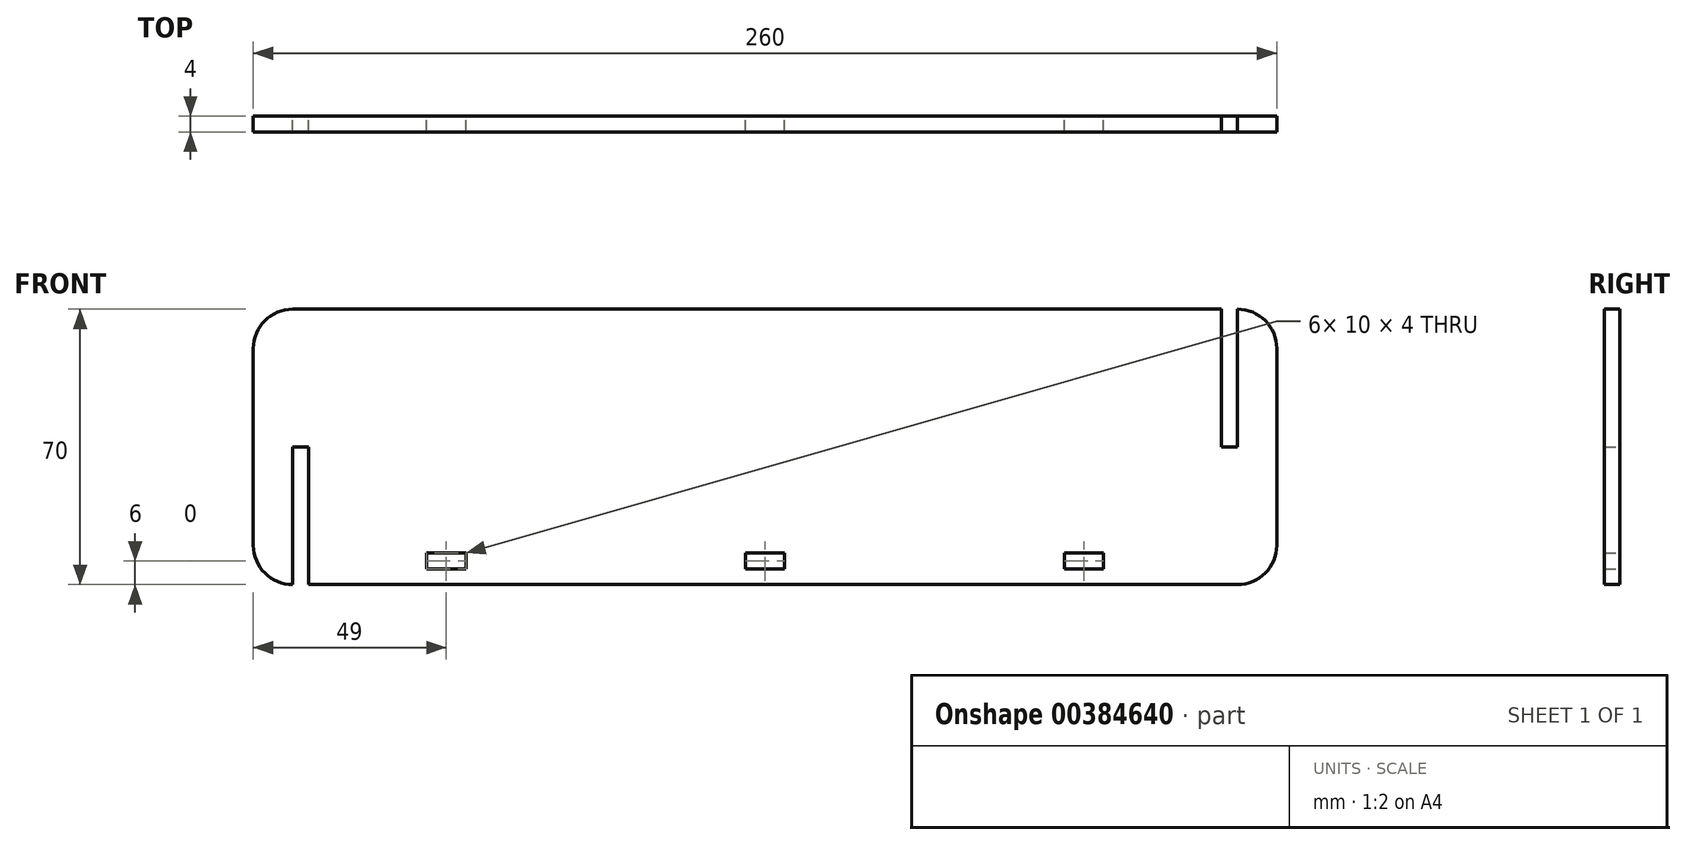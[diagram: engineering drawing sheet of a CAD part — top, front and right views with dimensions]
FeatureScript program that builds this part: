
annotation { "Feature Type Name" : "Feature", "Feature Type Description" : "" }
export const myFeature = defineFeature(function(context is Context, id is Id, definition is map)
    precondition{}
    {
        {
            var Q0;
            Q0=qCreatedBy(makeId("Front.planeOp"),FACE);
            var sketch = newSketch(context, id + "F0", { "sketchPlane" : qUnion([Q0])});
            skLineSegment(sketch, "E0.bottom", {"start": v(-120, 35) * mm, "end": v(116, 35) * mm});
            skLineSegment(sketch, "E0.top", {"start": v(-116, -35) * mm, "end": v(120, -35) * mm});
            skLineSegment(sketch, "E0.left", {"start": v(-130, 25) * mm, "end": v(-130, -25) * mm});
            skLineSegment(sketch, "E0.right", {"start": v(130, 25) * mm, "end": v(130, -25) * mm});
            skPoint(sketch, "E1.visualSharp", {"position": v(-130, 35) * mm});
            skArc(sketch, "E1.filletArc", {"start": v(-120, 35) * mm, "mid": v(-127.07, 32.07) * mm, "end": v(-130, 25) * mm});
            skPoint(sketch, "E2.visualSharp", {"position": v(-130, -35) * mm});
            skArc(sketch, "E2.filletArc", {"start": v(-130, -25) * mm, "mid": v(-127.07, -32.07) * mm, "end": v(-120, -35) * mm});
            skPoint(sketch, "E3.visualSharp", {"position": v(130, -35) * mm});
            skArc(sketch, "E3.filletArc", {"start": v(120, -35) * mm, "mid": v(127.07, -32.07) * mm, "end": v(130, -25) * mm});
            skPoint(sketch, "E4.visualSharp", {"position": v(130, 35) * mm});
            skArc(sketch, "E4.filletArc", {"start": v(130, 25) * mm, "mid": v(127.07, 32.07) * mm, "end": v(120, 35) * mm});
            skLineSegment(sketch, "E5.top", {"start": v(-120, 0) * mm, "end": v(-116, 0) * mm});
            skLineSegment(sketch, "E5.left", {"start": v(-120, -35) * mm, "end": v(-120, 0) * mm});
            skLineSegment(sketch, "E5.right", {"start": v(-116, -35) * mm, "end": v(-116, 0) * mm});
            skLineSegment(sketch, "E6.top", {"start": v(120, 0) * mm, "end": v(116, 0) * mm});
            skLineSegment(sketch, "E6.left", {"start": v(120, 35) * mm, "end": v(120, 0) * mm});
            skLineSegment(sketch, "E6.right", {"start": v(116, 35) * mm, "end": v(116, 0) * mm});
            skLineSegment(sketch, "E7.bottom", {"start": v(-86, -27) * mm, "end": v(-76, -27) * mm});
            skLineSegment(sketch, "E7.top", {"start": v(-86, -31) * mm, "end": v(-76, -31) * mm});
            skLineSegment(sketch, "E7.left", {"start": v(-86, -27) * mm, "end": v(-86, -31) * mm});
            skLineSegment(sketch, "E7.right", {"start": v(-76, -27) * mm, "end": v(-76, -31) * mm});
            skLineSegment(sketch, "E8.MirrorCS", {"start": v(76, -27) * mm, "end": v(76, -31) * mm});
            skLineSegment(sketch, "E9.MirrorCS", {"start": v(86, -31) * mm, "end": v(76, -31) * mm});
            skLineSegment(sketch, "E10.MirrorCS", {"start": v(86, -27) * mm, "end": v(76, -27) * mm});
            skLineSegment(sketch, "E11.MirrorCS", {"start": v(86, -27) * mm, "end": v(86, -31) * mm});
            skLineSegment(sketch, "E12.MirrorCS", {"start": v(-5, -27) * mm, "end": v(-5, -31) * mm});
            skLineSegment(sketch, "E13.MirrorCS", {"start": v(5, -31) * mm, "end": v(-5, -31) * mm});
            skLineSegment(sketch, "E14.MirrorCS", {"start": v(5, -27) * mm, "end": v(-5, -27) * mm});
            skLineSegment(sketch, "E15.MirrorCS", {"start": v(5, -27) * mm, "end": v(5, -31) * mm});
            skSolve(sketch);
        }
        {
            var Q0;
            Q0 = qSketchRegion(id + "F0", true);
            extrude(context, id + "F1", {"entities" : qUnion([Q0]), "depth" : 4 * mm});
        }
    });
